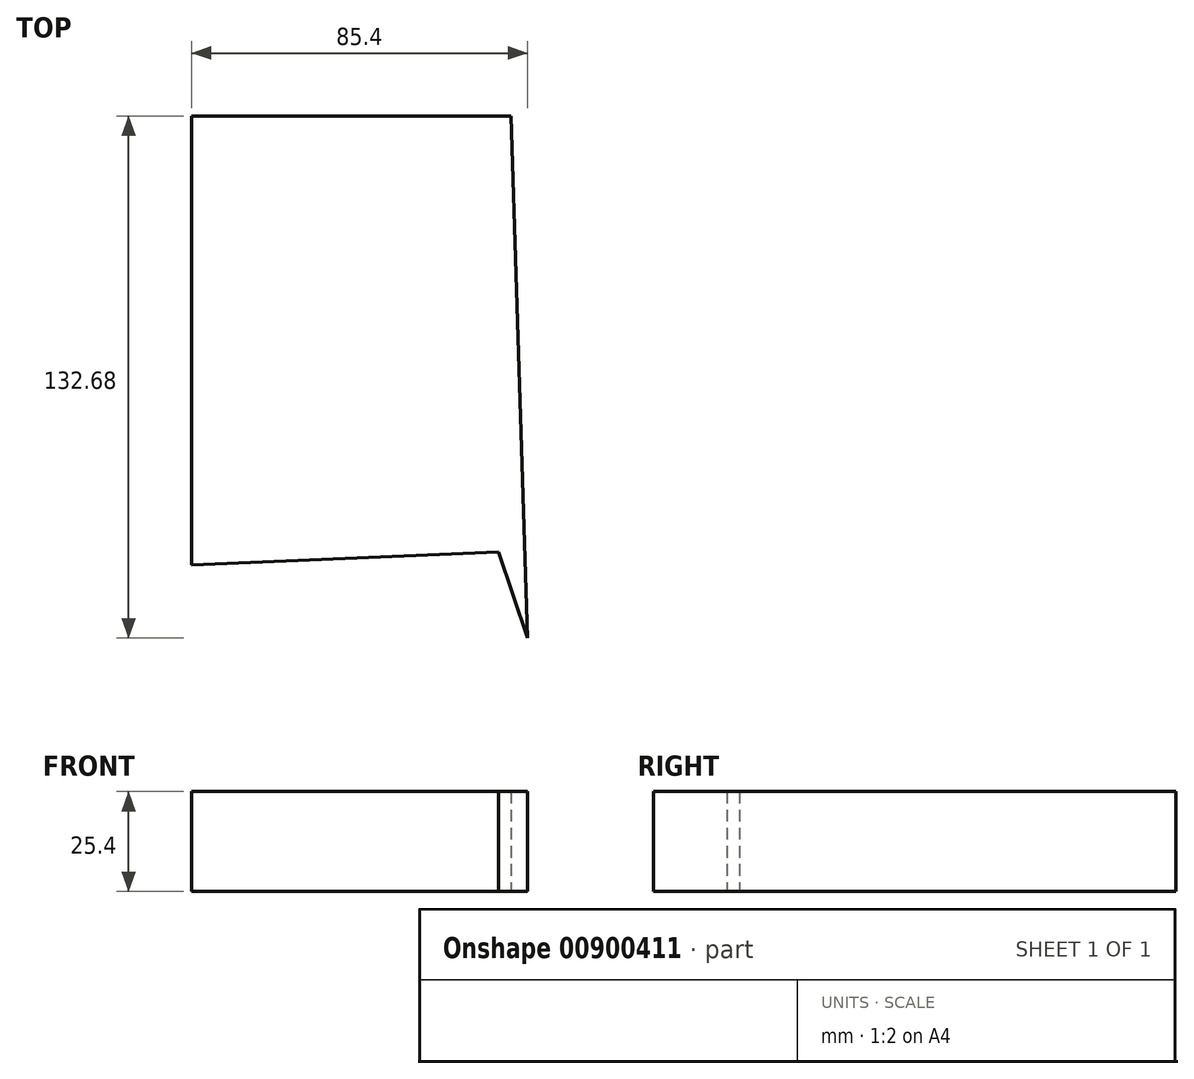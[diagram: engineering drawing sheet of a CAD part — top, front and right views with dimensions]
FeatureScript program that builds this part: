
annotation { "Feature Type Name" : "Feature", "Feature Type Description" : "" }
export const myFeature = defineFeature(function(context is Context, id is Id, definition is map)
    precondition{}
    {
        {
            var Q0;
            Q0=qCreatedBy(makeId("Top.planeOp"),FACE);
            var sketch = newSketch(context, id + "F0", { "sketchPlane" : qUnion([Q0])});
            skLineSegment(sketch, "E0", {"start": v(-81.13, -65.89) * mm, "end": v(-81.13, 48.15) * mm});
            skLineSegment(sketch, "E1", {"start": v(-81.13, 48.15) * mm, "end": v(0, 48.15) * mm});
            skLineSegment(sketch, "E2", {"start": v(0, 48.15) * mm, "end": v(4.27, -84.53) * mm});
            skLineSegment(sketch, "E3", {"start": v(4.27, -84.53) * mm, "end": v(-5.42, -56.15) * mm});
            skLineSegment(sketch, "E4", {"start": v(-3.19, -62.68) * mm, "end": v(-81.13, -65.89) * mm});
            skSolve(sketch);
        }
        {
            var Q0;
            Q0 = qSketchRegion(id + "F0", true);
            extrude(context, id + "F1", {"entities" : qUnion([Q0]), "depth" : 25.4 * mm, "offsetDistance" : 25.4 * mm});
        }
    });
